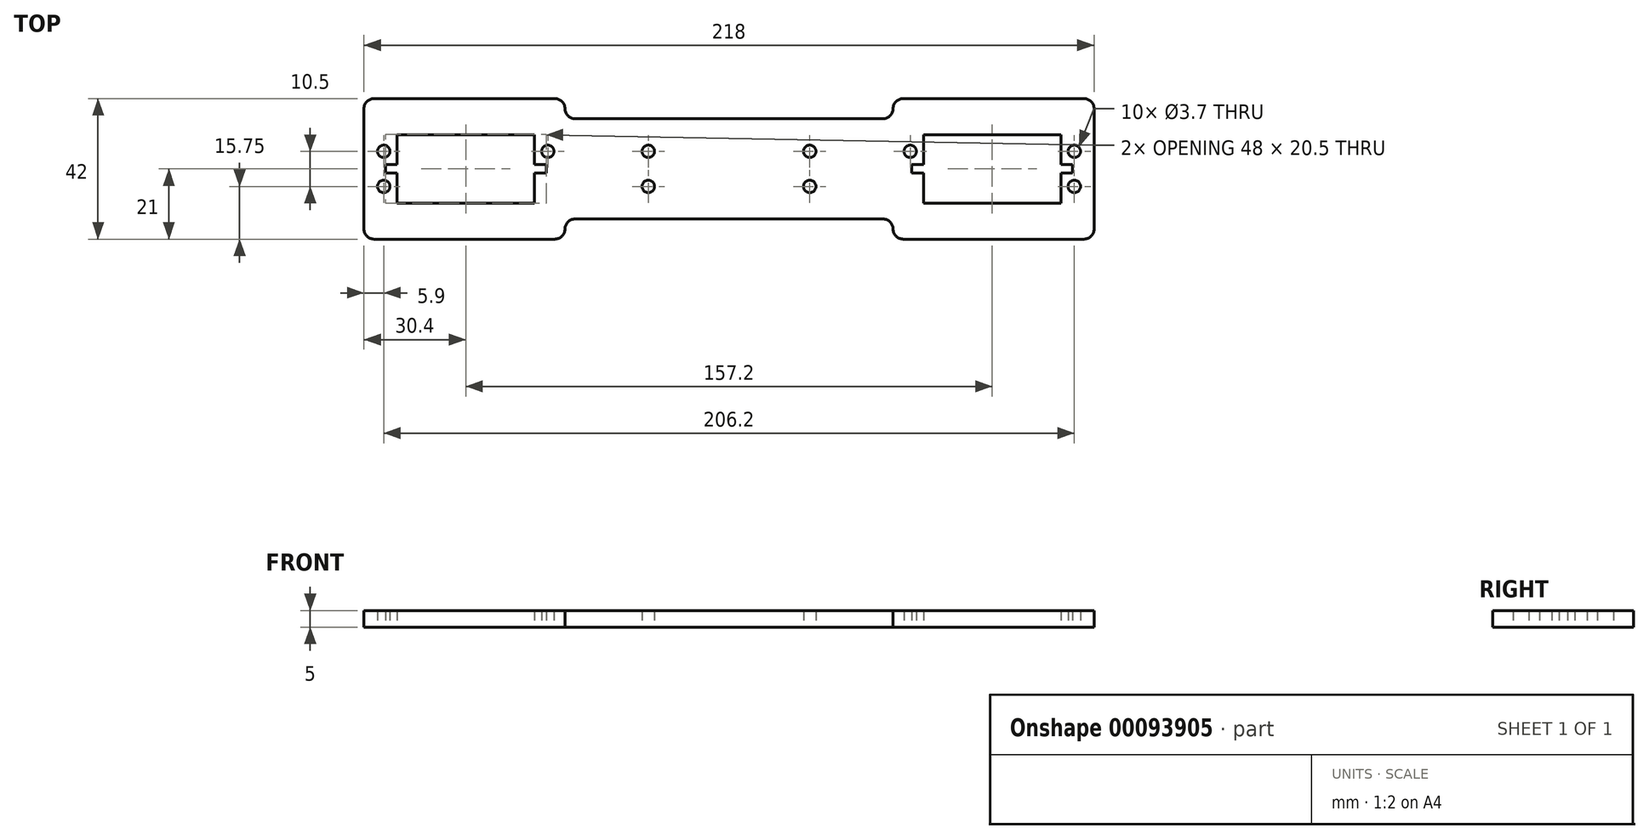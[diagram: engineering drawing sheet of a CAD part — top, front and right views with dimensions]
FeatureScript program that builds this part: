
annotation { "Feature Type Name" : "Feature", "Feature Type Description" : "" }
export const myFeature = defineFeature(function(context is Context, id is Id, definition is map)
    precondition{}
    {
        {
            var Q0;
            Q0=qCreatedBy(makeId("Top.planeOp"),FACE);
            var sketch = newSketch(context, id + "F0", { "sketchPlane" : qUnion([Q0])});
            skArc(sketch, "E0", {"start": v(106, -21) * mm, "mid": v(108.12, -20.12) * mm, "end": v(109, -18) * mm});
            skArc(sketch, "E1", {"start": v(109, 18) * mm, "mid": v(108.12, 20.12) * mm, "end": v(106, 21) * mm});
            skArc(sketch, "E2", {"start": v(52, 21) * mm, "mid": v(49.88, 20.12) * mm, "end": v(49, 18) * mm});
            skArc(sketch, "E3", {"start": v(49, -18) * mm, "mid": v(49.88, -20.12) * mm, "end": v(52, -21) * mm});
            skLineSegment(sketch, "E4", {"start": v(52, 21) * mm, "end": v(106, 21) * mm});
            skLineSegment(sketch, "E5", {"start": v(109, 18) * mm, "end": v(109, -18) * mm});
            skLineSegment(sketch, "E6", {"start": v(106, -21) * mm, "end": v(52, -21) * mm});
            skLineSegment(sketch, "E7.bottom", {"start": v(58.1, 10.25) * mm, "end": v(99.1, 10.25) * mm});
            skLineSegment(sketch, "E7.top", {"start": v(58.1, -10.25) * mm, "end": v(99.1, -10.25) * mm});
            skLineSegment(sketch, "E7.left", {"start": v(58.1, 10.25) * mm, "end": v(58.1, 1.25) * mm});
            skLineSegment(sketch, "E7.right", {"start": v(99.1, 10.25) * mm, "end": v(99.1, 1.25) * mm});
            skLineSegment(sketch, "E8.bottom", {"start": v(58.1, -1.25) * mm, "end": v(54.6, -1.25) * mm});
            skLineSegment(sketch, "E8.top", {"start": v(58.1, 1.25) * mm, "end": v(54.6, 1.25) * mm});
            skLineSegment(sketch, "E8.right", {"start": v(54.6, -1.25) * mm, "end": v(54.6, 1.25) * mm});
            skLineSegment(sketch, "E9.bottom", {"start": v(99.1, 1.25) * mm, "end": v(102.6, 1.25) * mm});
            skLineSegment(sketch, "E9.top", {"start": v(99.1, -1.25) * mm, "end": v(102.6, -1.25) * mm});
            skLineSegment(sketch, "E9.right", {"start": v(102.6, 1.25) * mm, "end": v(102.6, -1.25) * mm});
            skLineSegment(sketch, "E10.trimOffspring", {"start": v(99.1, -1.25) * mm, "end": v(99.1, -10.25) * mm});
            skLineSegment(sketch, "E11.trimOffspring", {"start": v(58.1, -1.25) * mm, "end": v(58.1, -10.25) * mm});
            skCircle(sketch, "E12", {"center": v(54.1, 5.25) * mm, "radius": 1.85 * mm});
            skCircle(sketch, "E13", {"center": v(194.1, -5.25) * mm, "radius": 1.5 * mm});
            skCircle(sketch, "E14", {"center": v(103.1, 5.25) * mm, "radius": 1.85 * mm});
            skCircle(sketch, "E15", {"center": v(103.1, -5.25) * mm, "radius": 1.85 * mm});
            skLineSegment(sketch, "E16", {"start": v(46, -15) * mm, "end": v(0, -15) * mm});
            skLineSegment(sketch, "E17", {"start": v(46, 15) * mm, "end": v(0, 15) * mm});
            skArc(sketch, "E18", {"start": v(46, 15) * mm, "mid": v(48.12, 15.88) * mm, "end": v(49, 18) * mm});
            skArc(sketch, "E19", {"start": v(49, -18) * mm, "mid": v(48.12, -15.88) * mm, "end": v(46, -15) * mm});
            skCircle(sketch, "E20", {"center": v(187.6, 0) * mm, "radius": 1.5 * mm});
            skPoint(sketch, "E20.centerSnap0", {"position": v(49, 0) * mm});
            skLineSegment(sketch, "E21.MirrorCS", {"start": v(-102.6, 1.25) * mm, "end": v(-102.6, -1.25) * mm});
            skLineSegment(sketch, "E22.MirrorCS", {"start": v(-58.1, 1.25) * mm, "end": v(-54.6, 1.25) * mm});
            skLineSegment(sketch, "E23.MirrorCS", {"start": v(-58.1, -1.25) * mm, "end": v(-54.6, -1.25) * mm});
            skLineSegment(sketch, "E24.MirrorCS", {"start": v(-99.1, -1.25) * mm, "end": v(-102.6, -1.25) * mm});
            skLineSegment(sketch, "E25.MirrorCS", {"start": v(-99.1, 1.25) * mm, "end": v(-102.6, 1.25) * mm});
            skLineSegment(sketch, "E26.MirrorCS", {"start": v(-54.6, -1.25) * mm, "end": v(-54.6, 1.25) * mm});
            skCircle(sketch, "E27.MirrorC", {"center": v(-187.6, 0) * mm, "radius": 1.5 * mm});
            skPoint(sketch, "E28.MirrorP", {"position": v(-49, 0) * mm});
            skLineSegment(sketch, "E29.MirrorCS", {"start": v(-58.1, -1.25) * mm, "end": v(-58.1, -10.25) * mm});
            skCircle(sketch, "E30.MirrorC", {"center": v(-194.1, -5.25) * mm, "radius": 1.5 * mm});
            skCircle(sketch, "E31.MirrorC", {"center": v(-103.1, -5.25) * mm, "radius": 1.85 * mm});
            skLineSegment(sketch, "E32.MirrorCS", {"start": v(-46, -15) * mm, "end": v(0, -15) * mm});
            skArc(sketch, "E33.MirrorCS", {"start": v(-46, 15) * mm, "mid": v(-48.12, 15.88) * mm, "end": v(-49, 18) * mm});
            skLineSegment(sketch, "E34.MirrorCS", {"start": v(-99.1, 10.25) * mm, "end": v(-99.1, 1.25) * mm});
            skLineSegment(sketch, "E35.MirrorCS", {"start": v(-58.1, 10.25) * mm, "end": v(-58.1, 1.25) * mm});
            skLineSegment(sketch, "E36.MirrorCS", {"start": v(-58.1, -10.25) * mm, "end": v(-99.1, -10.25) * mm});
            skLineSegment(sketch, "E37.MirrorCS", {"start": v(-58.1, 10.25) * mm, "end": v(-99.1, 10.25) * mm});
            skLineSegment(sketch, "E38.MirrorCS", {"start": v(-106, -21) * mm, "end": v(-52, -21) * mm});
            skLineSegment(sketch, "E39.MirrorCS", {"start": v(-109, 18) * mm, "end": v(-109, -18) * mm});
            skLineSegment(sketch, "E40.MirrorCS", {"start": v(-52, 21) * mm, "end": v(-106, 21) * mm});
            skArc(sketch, "E41.MirrorCS", {"start": v(-49, -18) * mm, "mid": v(-49.88, -20.12) * mm, "end": v(-52, -21) * mm});
            skArc(sketch, "E42.MirrorCS", {"start": v(-52, 21) * mm, "mid": v(-49.88, 20.12) * mm, "end": v(-49, 18) * mm});
            skArc(sketch, "E43.MirrorCS", {"start": v(-109, 18) * mm, "mid": v(-108.12, 20.12) * mm, "end": v(-106, 21) * mm});
            skArc(sketch, "E44.MirrorCS", {"start": v(-106, -21) * mm, "mid": v(-108.12, -20.12) * mm, "end": v(-109, -18) * mm});
            skLineSegment(sketch, "E45.MirrorCS", {"start": v(-46, 15) * mm, "end": v(0, 15) * mm});
            skLineSegment(sketch, "E46.MirrorCS", {"start": v(-99.1, -1.25) * mm, "end": v(-99.1, -10.25) * mm});
            skCircle(sketch, "E47.MirrorC", {"center": v(-54.1, 5.25) * mm, "radius": 1.85 * mm});
            skCircle(sketch, "E48.MirrorC", {"center": v(-103.1, 5.25) * mm, "radius": 1.85 * mm});
            skArc(sketch, "E49.MirrorCS", {"start": v(-49, -18) * mm, "mid": v(-48.12, -15.88) * mm, "end": v(-46, -15) * mm});
            skCircle(sketch, "E50", {"center": v(-24.1, 5.25) * mm, "radius": 1.85 * mm});
            skCircle(sketch, "E51", {"center": v(-24.1, -5.25) * mm, "radius": 1.85 * mm});
            skCircle(sketch, "E52", {"center": v(24.1, 5.25) * mm, "radius": 1.85 * mm});
            skCircle(sketch, "E53", {"center": v(24.1, -5.25) * mm, "radius": 1.85 * mm});
            skSolve(sketch);
        }
        {
            var Q0;
            Q0=makeQuery(id+"F0.imprint","IMPRINT",FACE,{"disambiguationData":[TD([[makeQuery(id+"F0.imprint","IMPRINT",EDGE,{"derivedFrom":sQuery(id+"F0.wireOp",EDGE,"E0")}),1.0]])]});
            extrude(context, id + "F1", {"entities" : qUnion([Q0]), "depth" : 5 * mm});
        }
    });
